# Revit family: Tub_Filler-Grohe-Essence-23491_Series
name_source: partatom
category: Plumbing Fixtures
revit_build: Autodesk Revit 2015 (Build: 20140606_1530(x64)
units: mm (PartAtom-declared; Revit-internal decimal feet)

## types (4) — shared parameters
Assembly Code = D2020300
CW Connection = Yes
CWFU = 3
Cold Water Connection Diameter = 1/2"
Default Elevation = 0"
Description = Essence Floor Standing Tub Filler
Flow Rate = 2.0 gpm (7.6 L/min)
HW Connection = Yes
HWFU = 3
Height = 30 11/16"
Hot Water Connection Diameter = 1"
Installation Type = Floor Mounted
Length = 10 7/8"
Manufacturer = Grohe
Price = Prices may vary. Please consult Manufacturer Representative for most up-to-date price list.
Product Page URL = https://www.grohe.us
Tempered Water Connection Diameter = 1/2"
URL = https://www.grohe.us
Vent Connection = No
WFU = 4
Warranty Information = Limited Lifetime Warranty
Waste Connection = No
Width = 6 11/16"

## per-type parameters (varying)
| type | Finish | Material |
| 23491A0A | Metal-Grohe-A0A-Hard Graphite | Metal-Grohe-A0A-Hard Graphite |
| 23491BEA | Metal-Grohe-BEA-Polished Nickel | Metal-Grohe-BEA-Polished Nickel |
| 23491GNA | Metal-Grohe-GNA-Brushed Cool Sunset | Metal-Grohe-GNA-Brushed Cool Sunset |
| 23491EN1 | Metal-Grohe-EN1-Brushed Nickel | Metal-Grohe-EN1-Brushed Nickel |

note: column(s) folded — value = type name in every type: Model

## geometry (parser evidence)
native form markers: Sweep x1
no freeform markers — native parametric forms only
